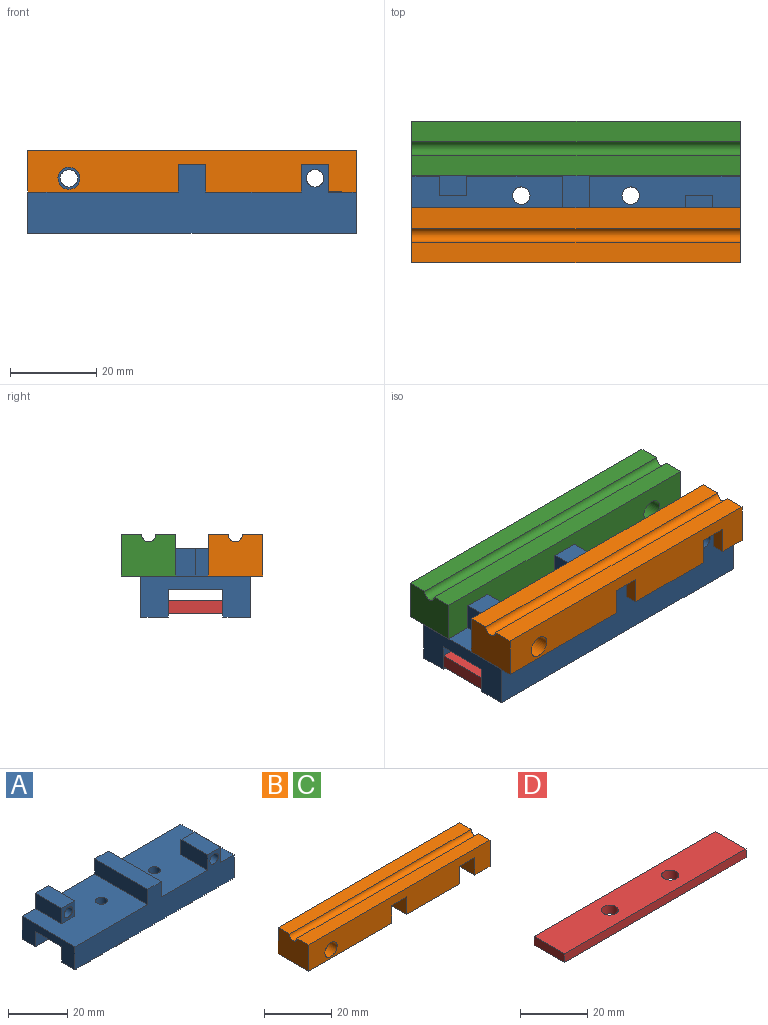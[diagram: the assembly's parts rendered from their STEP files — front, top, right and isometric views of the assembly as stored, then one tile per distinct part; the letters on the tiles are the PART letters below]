
ASSEMBLY  parts=4 mates=5
PART A: 26 faces, bbox 76.2x25.4x15.9 mm
  f0: plane 34.93x25.4mm, normal (0,0,1), area 793.6mm2, adj f1,f9,f13,f14,f16,f17,f21,f25
  f1: plane 76.2x15.88mm, normal (0,1,0), area 793.6mm2, adj f0,f7,f8,f12,f13,f14,f15,f16
  f2: plane 12.7x6.35mm, normal (1,0,0), area 80.6mm2, adj f3,f8,f9,f18
  f3: plane 12.7x6.35mm, normal (0,0,1), area 80.6mm2, adj f2,f4,f9,f18
  f4: plane 12.7x6.35mm, normal (-1,0,0), area 80.6mm2, adj f3,f8,f9,f18
  f5: plane 76.2x12.7mm, normal (0,0,-1), area 942.1mm2, adj f6,f11,f12,f13,f21,f22
  f6: plane 76.2x6.35mm, normal (0,-1,0), area 483.9mm2, adj f5,f7,f12,f13
  f7: plane 76.2x6.35mm, normal (0,0,-1), area 483.9mm2, adj f1,f6,f12,f13
  f8: plane 34.93x25.4mm, normal (0,0,1), area 793.6mm2, adj f1,f2,f4,f9,f12,f18,f22,f23
  f9: plane 76.2x15.88mm, normal (0,-1,0), area 793.6mm2, adj f0,f2,f3,f4,f8,f10,f12,f13
  f10: plane 76.2x6.35mm, normal (0,0,-1), area 483.9mm2, adj f9,f11,f12,f13
  f11: plane 76.2x6.35mm, normal (0,1,0), area 483.9mm2, adj f5,f10,f12,f13
  f12: plane 25.4x9.53mm, normal (1,0,0), area 161.3mm2, adj f1,f5,f6,f7,f8,f9,f10,f11
  f13: plane 25.4x9.53mm, normal (-1,0,0), area 161.3mm2, adj f0,f1,f5,f6,f7,f9,f10,f11
  f14: plane 12.7x6.35mm, normal (1,0,0), area 80.6mm2, adj f0,f1,f15,f17
  f15: plane 12.7x6.35mm, normal (0,0,1), area 80.6mm2, adj f1,f14,f16,f17
  f16: plane 12.7x6.35mm, normal (-1,0,0), area 80.6mm2, adj f0,f1,f15,f17
  f17: plane 6.35x6.35mm, normal (0,-1,0), area 27.5mm2, adj f0,f14,f15,f16,f20
  f18: plane 6.35x6.35mm, normal (0,1,0), area 27.5mm2, adj f2,f3,f4,f8,f19
  f19: cylinder r=2.02mm len=12.7mm, axis (0,1,0), area 161.1mm2, adj f9,f18
  f20: cylinder r=2.02mm len=12.7mm, axis (0,-1,0), area 161.1mm2, adj f1,f17
  f21: cylinder r=2.02mm len=4.04mm, axis (0,0,1), area 40.3mm2, adj f0,f5
  f22: cylinder r=2.02mm len=4.04mm, axis (0,0,1), area 40.3mm2, adj f5,f8
  f23: plane 25.4x6.35mm, normal (1,0,0), area 161.3mm2, adj f1,f8,f9,f24
  f24: plane 25.4x6.35mm, normal (0,0,1), area 161.3mm2, adj f1,f9,f23,f25
  f25: plane 25.4x6.35mm, normal (-1,0,0), area 161.3mm2, adj f0,f1,f9,f24
PART B: 17 faces, bbox 76.2x12.7x9.5 mm
  f0: plane 76.2x4.76mm, normal (0,0,1), area 362.9mm2, adj f1,f7,f13,f15
  f1: plane 12.7x9.53mm, normal (-1,0,0), area 117mm2, adj f0,f8,f9,f13,f14,f15
  f2: plane 22.23x12.7mm, normal (0,0,-1), area 282.3mm2, adj f3,f12,f13,f14
  f3: plane 12.7x6.35mm, normal (1,0,0), area 80.6mm2, adj f2,f4,f13,f14
  f4: plane 12.7x6.35mm, normal (0,0,-1), area 80.6mm2, adj f3,f5,f13,f14
  f5: plane 12.7x6.35mm, normal (-1,0,0), area 80.6mm2, adj f4,f6,f13,f14
  f6: plane 12.7x6.35mm, normal (0,0,-1), area 80.6mm2, adj f5,f7,f13,f14
  f7: plane 12.7x9.53mm, normal (1,0,0), area 117mm2, adj f0,f6,f8,f13,f14,f15
  f8: plane 76.2x4.76mm, normal (0,0,1), area 362.9mm2, adj f1,f7,f14,f15
  f9: plane 34.93x12.7mm, normal (0,0,-1), area 443.5mm2, adj f1,f10,f13,f14
  f10: plane 12.7x6.35mm, normal (1,0,0), area 80.6mm2, adj f9,f11,f13,f14
  f11: plane 12.7x6.35mm, normal (0,0,-1), area 80.6mm2, adj f10,f12,f13,f14
  f12: plane 12.7x6.35mm, normal (-1,0,0), area 80.6mm2, adj f2,f11,f13,f14
  f13: plane 76.2x9.53mm, normal (0,1,0), area 624.7mm2, adj f0,f1,f2,f3,f4,f5,f6,f7
  f14: plane 76.2x9.53mm, normal (0,-1,0), area 624.7mm2, adj f1,f2,f3,f4,f5,f6,f7,f8
  f15: cylinder r=1.59mm len=76.2mm, axis (1,0,0), area 380mm2, adj f0,f1,f7,f8
  f16: cylinder r=2.55mm len=12.7mm, axis (0,-1,0), area 203.7mm2, adj f13,f14
PART C: same geometry as B
PART D: 8 faces, bbox 76.2x12.7x3.2 mm
  f0: plane 76.2x12.7mm, normal (0,0,1), area 926.8mm2, adj f1,f3,f4,f5,f6,f7
  f1: plane 76.2x3.18mm, normal (0,-1,0), area 241.9mm2, adj f0,f2,f4,f5
  f2: plane 76.2x12.7mm, normal (0,0,-1), area 926.8mm2, adj f1,f3,f4,f5,f6,f7
  f3: plane 76.2x3.18mm, normal (0,1,0), area 241.9mm2, adj f0,f2,f4,f5
  f4: plane 12.7x3.18mm, normal (1,0,0), area 40.3mm2, adj f0,f1,f2,f3
  f5: plane 12.7x3.18mm, normal (-1,0,0), area 40.3mm2, adj f0,f1,f2,f3
  f6: cylinder r=2.55mm len=5.11mm, axis (0,0,1), area 50.9mm2, adj f0,f2
  f7: cylinder r=2.55mm len=5.11mm, axis (0,0,1), area 50.9mm2, adj f0,f2
PLACE A t=(-28.01,12.53,12.32)mm fixed
PLACE B t=(10.09,-3.06,21.85)mm
PLACE C rot(axis=(0,0,-1),180deg) t=(10.09,29.79,21.85)mm
PLACE D t=(-28.01,6.18,13.03)mm
MATE planar B.f2 <-> A.f8  axis (0,0,-1) through (24.37,3.29,21.85)mm
MATE planar B.f5 <-> A.f2  axis (-1,0,0) through (41.84,3.29,25.02)mm
MATE planar C.f2 <-> A.f0  axis (0,0,-1) through (-4.2,23.44,21.85)mm
MATE planar C.f3 <-> A.f14  axis (-1,0,0) through (-15.31,23.44,25.02)mm
MATE slider D.f7 <-> A.f22  axis (0,0,1) through (22.79,12.53,16.21)mm
